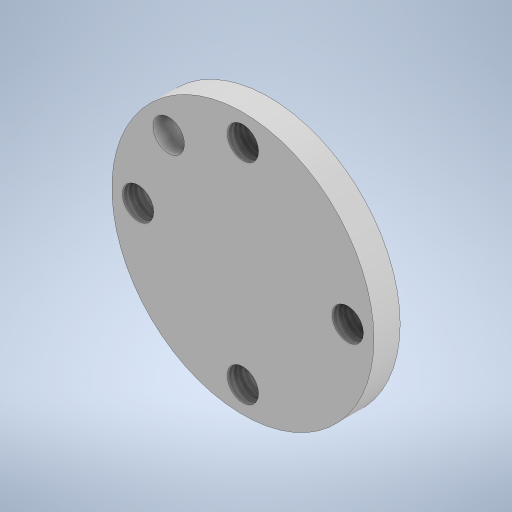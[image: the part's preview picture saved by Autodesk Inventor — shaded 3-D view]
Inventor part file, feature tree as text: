
AUTODESK INVENTOR PART (.ipt)
format: ipt  version: 2023 (Build 270158000, 158)  size: 254,464 bytes
history: native  units: mm
features: thread x4, sketch x4, extrude x2, hole x1, pattern_circular x1
ambient origin geometry x8: Origin, YZ Plane, XZ Plane, XY Plane, X Axis, Y Axis, Z Axis, Center Point
bodies: Solid1 (feature_tree)
feature tree (12):
  extrude  "Extrusion1"  Depth=5.0mm TaperAngle=0.0deg
  hole  "Hole1"  [1 undecoded]
  thread  "Thread1"  [1 undecoded]
  thread  "Thread2"  [1 undecoded]
  thread  "Thread3"  [1 undecoded]
  thread  "Thread4"  [1 undecoded]
  sketch  "Sketch3"  dims[d8=6.0mm d9=6.0mm d10=4.0mm d11=2.0mm d12=90.0deg d13=8.0mm d14=20.594885mm d15=10.0mm d16=0.0mm d17=10.0mm d18=0.0mm]
  pattern_circular  "Circular Pattern1"  [2 undecoded]
  extrude  "Extrusion2"  Depth=5.0mm TaperAngle=45.0deg
  sketch  "Sketch1"  dims[d0=50.0mm d1=5.0mm d2=0.0mm]
  sketch  "Sketch2"  dims[d4=6.0mm d5=6.0mm d6=6.0mm d7=6.0mm]
  sketch  "Sketch4"  dims[d19=10.0mm d20=0.0mm d21=10.0mm d22=0.0mm d24=20.0mm d25=45.0deg d27=5.0mm d28=0.0mm]
note: 7 required parameter values undecoded (feature->parameter linkage not recoverable at this tier; creation-order binding heuristic only, values carry confidence <= 0.55)
